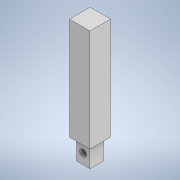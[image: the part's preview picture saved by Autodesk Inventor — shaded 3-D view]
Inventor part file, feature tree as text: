
AUTODESK INVENTOR PART (.ipt)
format: ipt  version: 2021 (Build 250183000, 183)  size: 116,224 bytes
history: native  units: in
note: dims shown in document units (in); Inventor stores cm internally (conversion verified against a paired STEP export)
features: sketch x3, extrude x2, hole x1
ambient origin geometry x8: Origin, YZ Plane, XZ Plane, XY Plane, X Axis, Y Axis, Z Axis, Center Point
bodies: Solid1 (feature_tree)
feature tree (6):
  extrude  "Extrusion1"  Depth=0.3937in
  extrude  "Extrusion2"  Depth=0.5906in
  hole  "Hole1"  [1 undecoded]
  sketch  "Sketch1"  dims[d0=0.3937in d1=0.3937in]
  sketch  "Sketch2"  dims[d2=0.5906in d3=0.0in d4=0.5906in]
  sketch  "Sketch3"  dims[d5=0.5906in d6=2.9528in d7=0.0in d8=0.1969in d9=0.2362in d10=0.1575in d11=0.0787in d12=90.0deg d13=0.315in d14=0.8108in d15=0.0295in d16=0.8108in d17=0.0025in d18=0.0295in d19=0.0148in]
note: 1 required parameter value undecoded (feature->parameter linkage not recoverable at this tier; creation-order binding heuristic only, values carry confidence <= 0.55)
